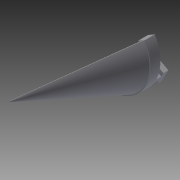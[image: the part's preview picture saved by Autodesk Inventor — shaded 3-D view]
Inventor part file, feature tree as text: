
AUTODESK INVENTOR PART (.ipt)
format: ipt  version: 2015 (Build 190159000, 159)  size: 125,440 bytes
history: native  units: mm
features: sketch x3, extrude x2, revolve x1
ambient origin geometry x8: Origin, YZ Plane, XZ Plane, XY Plane, X Axis, Y Axis, Z Axis, Center Point
bodies: Solid1 (feature_tree)
feature tree (6):
  revolve  "Revolution1"  [1 undecoded]
  extrude  "Extrusion1"  Depth=2.0mm
  extrude  "Extrusion2"  Depth=10.0mm
  sketch  "Sketch1"  dims[d0=100.0mm d1=40.0mm]
  sketch  "Sketch2"  dims[d2=1.0mm d3=2.0mm]
  sketch  "Sketch3"  dims[d7=1.0mm d8=10.0mm d9=8.0mm d10=120.0deg d11=3.0mm d12=3.0mm d13=15.0mm d14=6.0mm d15=20.0mm d16=0.0mm d17=7.5mm d18=5.0mm d19=15.0mm d20=15.0mm d21=0.0mm]
note: 1 required parameter value undecoded (feature->parameter linkage not recoverable at this tier; creation-order binding heuristic only, values carry confidence <= 0.55)
